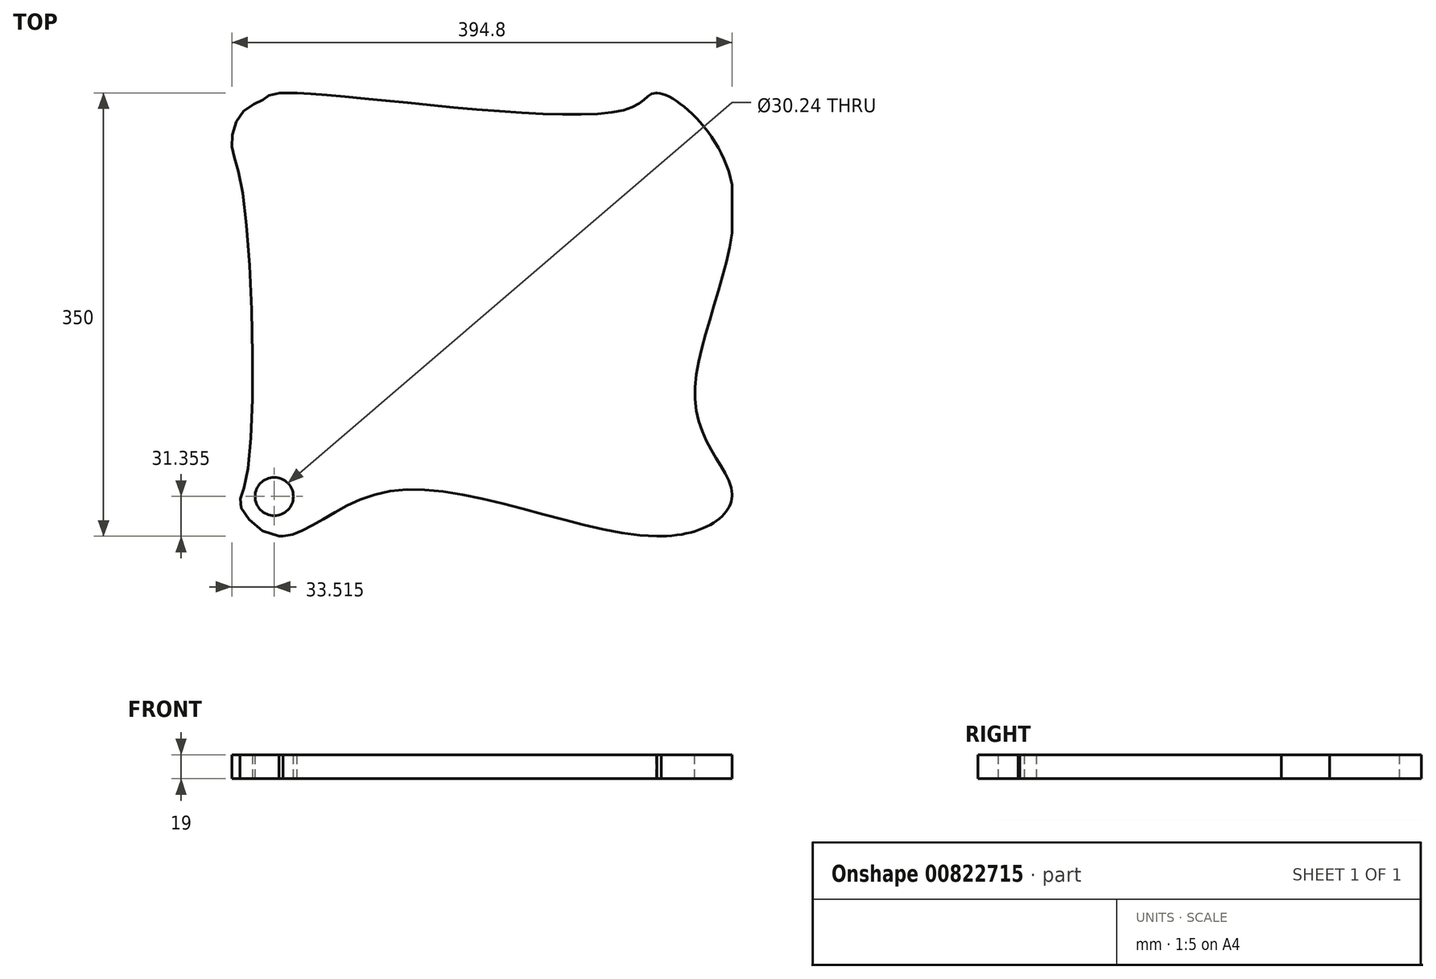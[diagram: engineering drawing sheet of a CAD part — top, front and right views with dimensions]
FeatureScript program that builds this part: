
annotation { "Feature Type Name" : "Feature", "Feature Type Description" : "" }
export const myFeature = defineFeature(function(context is Context, id is Id, definition is map)
    precondition{}
    {
        {
            var Q0;
            Q0=qCreatedBy(makeId("Top.planeOp"),FACE);
            var sketch = newSketch(context, id + "F0", { "sketchPlane" : qUnion([Q0])});
            skLineSegment(sketch, "E0.bottom", {"start": v(-200, -175) * mm, "end": v(200, -175) * mm});
            skLineSegment(sketch, "E0.top", {"start": v(-200, 175) * mm, "end": v(200, 175) * mm});
            skLineSegment(sketch, "E0.left", {"start": v(-200, -175) * mm, "end": v(-200, 175) * mm});
            skLineSegment(sketch, "E0.right", {"start": v(200, -175) * mm, "end": v(200, 175) * mm});
            skPoint(sketch, "E0.middle", {"position": v(0, 0) * mm});
            skSolve(sketch);
        }
        {
            var Q0;
            Q0 = qSketchRegion(id + "F0", true);
            extrude(context, id + "F1", {"entities" : qUnion([Q0]), "depth" : 19 * mm, "offsetDistance" : 25 * mm});
        }
        {
            var Q0;
            Q0=makeQuery(id+"F1.opExtrude","CAP_FACE",FACE,{"disambiguationData":[OSD([sQuery(id+"F0.wireOp",EDGE,"E0.bottom"),sQuery(id+"F0.wireOp",EDGE,"E0.top"),sQuery(id+"F0.wireOp",EDGE,"E0.left"),sQuery(id+"F0.wireOp",EDGE,"E0.right")])],"isStart":false});
            var sketch = newSketch(context, id + "F2", { "sketchPlane" : qUnion([Q0])});
            skFitSpline(sketch, "E1", {"points": [v(-156.85, 175) * mm, v(-169.74, 170.01) * mm, v(-186.43, 159.74) * mm, v(-194.78, 134.7) * mm, v(-187.08, 101.97) * mm, v(-183.22, -129.13) * mm, v(-187.72, -151.6) * mm, v(-157.55, -175) * mm, v(-70.24, -139.4) * mm, v(144.16, -175) * mm, v(200, -143.25) * mm, v(171.12, -72.64) * mm, v(200, 102.6) * mm, v(140.95, 175) * mm, v(115.27, 161.67) * mm, v(-156.85, 175) * mm]});
            skCircle(sketch, "E2", {"center": v(-161.29, -143.64) * mm, "radius": 15.12 * mm});
            skSolve(sketch);
        }
        {
            var Q0;
            {var subQ0=sQuery(id+"F2.wireOp",EDGE,"E1");var subQ1=makeQuery(id+"F1.opExtrude","CAP_EDGE",EDGE,{"disambiguationData":[OSD([sQuery(id+"F0.wireOp",EDGE,"E0.top")])],"isStart":false});var subQ2=makeQuery(id+"F2.imprint","INTERSECT",VERTEX,{"disambiguationData":[OD(2.0)],"derivedFrom":[subQ1,subQ0]});Q0=makeQuery(id+"F2.imprint","IMPRINT",FACE,{"disambiguationData":[TD([[makeQuery(id+"F2.imprint","IMPRINT",EDGE,{"disambiguationData":[TD([[subQ2,-1.0]])],"derivedFrom":subQ0}),-1.0]])]});}
            var Q1;
            {var subQ0=sQuery(id+"F2.wireOp",EDGE,"E1");var subQ1=makeQuery(id+"F1.opExtrude","CAP_EDGE",EDGE,{"disambiguationData":[OSD([sQuery(id+"F0.wireOp",EDGE,"E0.right")])],"isStart":false});var subQ2=makeQuery(id+"F2.imprint","INTERSECT",VERTEX,{"disambiguationData":[OD(3.0)],"derivedFrom":[subQ1,subQ0]});Q1=makeQuery(id+"F2.imprint","IMPRINT",FACE,{"disambiguationData":[TD([[makeQuery(id+"F2.imprint","IMPRINT",EDGE,{"disambiguationData":[TD([[subQ2,-1.0]])],"derivedFrom":subQ0}),-1.0]])]});}
            var Q2;
            {var subQ0=sQuery(id+"F2.wireOp",EDGE,"E1");var subQ1=makeQuery(id+"F1.opExtrude","CAP_EDGE",EDGE,{"disambiguationData":[OSD([sQuery(id+"F0.wireOp",EDGE,"E0.right")])],"isStart":false});var subQ2=makeQuery(id+"F2.imprint","INTERSECT",VERTEX,{"disambiguationData":[OD(1.0)],"derivedFrom":[subQ1,subQ0]});Q2=makeQuery(id+"F2.imprint","IMPRINT",FACE,{"disambiguationData":[TD([[makeQuery(id+"F2.imprint","IMPRINT",EDGE,{"disambiguationData":[TD([[subQ2,-1.0]])],"derivedFrom":subQ0}),-1.0]])]});}
            var Q3;
            {var subQ0=sQuery(id+"F2.wireOp",EDGE,"E1");var subQ1=makeQuery(id+"F1.opExtrude","CAP_EDGE",EDGE,{"disambiguationData":[OSD([sQuery(id+"F0.wireOp",EDGE,"E0.bottom")])],"isStart":false});var subQ2=makeQuery(id+"F2.imprint","INTERSECT",VERTEX,{"disambiguationData":[OD(3.0)],"derivedFrom":[subQ1,subQ0]});Q3=makeQuery(id+"F2.imprint","IMPRINT",FACE,{"disambiguationData":[TD([[makeQuery(id+"F2.imprint","IMPRINT",EDGE,{"disambiguationData":[TD([[subQ2,-1.0]])],"derivedFrom":subQ0}),-1.0]])]});}
            var Q4;
            {var subQ0=sQuery(id+"F2.wireOp",EDGE,"E1");var subQ1=makeQuery(id+"F1.opExtrude","CAP_EDGE",EDGE,{"disambiguationData":[OSD([sQuery(id+"F0.wireOp",EDGE,"E0.bottom")])],"isStart":false});var subQ2=makeQuery(id+"F2.imprint","INTERSECT",VERTEX,{"disambiguationData":[OD(1.0)],"derivedFrom":[subQ1,subQ0]});Q4=makeQuery(id+"F2.imprint","IMPRINT",FACE,{"disambiguationData":[TD([[makeQuery(id+"F2.imprint","IMPRINT",EDGE,{"disambiguationData":[TD([[subQ2,-1.0]])],"derivedFrom":subQ0}),-1.0]])]});}
            var Q5;
            {var subQ5=makeQuery(id+"F1.opExtrude","CAP_EDGE",EDGE,{"disambiguationData":[OSD([sQuery(id+"F0.wireOp",EDGE,"E0.left")])],"isStart":false});Q5=makeQuery(id+"F2.imprint","IMPRINT",FACE,{"disambiguationData":[TD([[makeQuery(id+"F2.imprint","IMPRINT",EDGE,{"derivedFrom":subQ5}),-1.0]])]});}
            extrude(context, id + "F3", {"entities" : qUnion([Q0, Q1, Q2, Q3, Q4, Q5]), "operationType" : NewBodyOperationType.REMOVE, "endBound" : BoundingType.THROUGH_ALL, "oppositeDirection" : true, "depth" : 50 * mm, "offsetDistance" : 25 * mm});
        }
        {
            var Q0;
            Q0=makeQuery(id+"F2.imprint","IMPRINT",FACE,{"disambiguationData":[TD([[makeQuery(id+"F2.imprint","IMPRINT",EDGE,{"derivedFrom":sQuery(id+"F2.wireOp",EDGE,"E2")}),1.0]])]});
            extrude(context, id + "F4", {"entities" : qUnion([Q0]), "operationType" : NewBodyOperationType.REMOVE, "endBound" : BoundingType.THROUGH_ALL, "oppositeDirection" : true, "depth" : 282 * mm, "offsetDistance" : 25 * mm});
        }
    });
